# Revit family: 202_Fondue-E
name_source: partatom
category: Air Terminals
revit_build: Autodesk Revit 2018 (Build: 20170223_1515(x64)
units: mm (PartAtom-declared; Revit-internal decimal feet)

## family parameters
Always vertical = Yes
Cut with Voids When Loaded = No
Part Type = Normal
Room Calculation Point = Yes
Round Connector Dimension = Use Diameter
Shared = No
Work Plane-Based = No

## types (1)
- 125-13616
    CAT0 = Yes
    CLBTZ = 0 mm  [stored 0 ft]
    CL_Location_5000 = 5000 mm  [stored 16.4042 ft]
    D = 125 mm
    Description = Kitchen hood Fondue-E
    H1 = 19 mm  [stored 0.062336 ft]
    H1__ve = -19 mm  [stored -0.062336 ft]
    H3 = 101 mm  [stored 0.331365 ft]
    H_ARR = 0 mm  [stored 0 ft]
    L2 = 310 mm  [stored 1.01706 ft]
    L3 = 221 mm  [stored 0.725066 ft]
    L4 = 39 mm
    L5 = 299 mm  [stored 0.980971 ft]
    L_ARR = 400 mm  [stored 1.31234 ft]
    MC Product Code = 125-13616
    Manufacturer = Flexit
    QmdConnectorList = 201;D
    W = 296 mm  [stored 0.971129 ft]
    W2 = 103 mm  [stored 0.337927 ft]
    W3 = 148 mm  [stored 0.485564 ft]
    W4 = 170 mm  [stored 0.557743 ft]
    W_ARR = 400 mm  [stored 1.31234 ft]
    XRefLineVPlnId = 7453
    YRefLineVPlnId = 7456
    magiPartTypeId = 202
    magiProductFamilyId = Fondue-E
    magiProductId = Fondue-E 125

note: [stored X ft] marks values corroborated as IEEE doubles in the binary element streams (Revit-internal decimal feet)

## geometry (parser evidence)
native form markers: Sweep x2
no freeform markers — native parametric forms only
